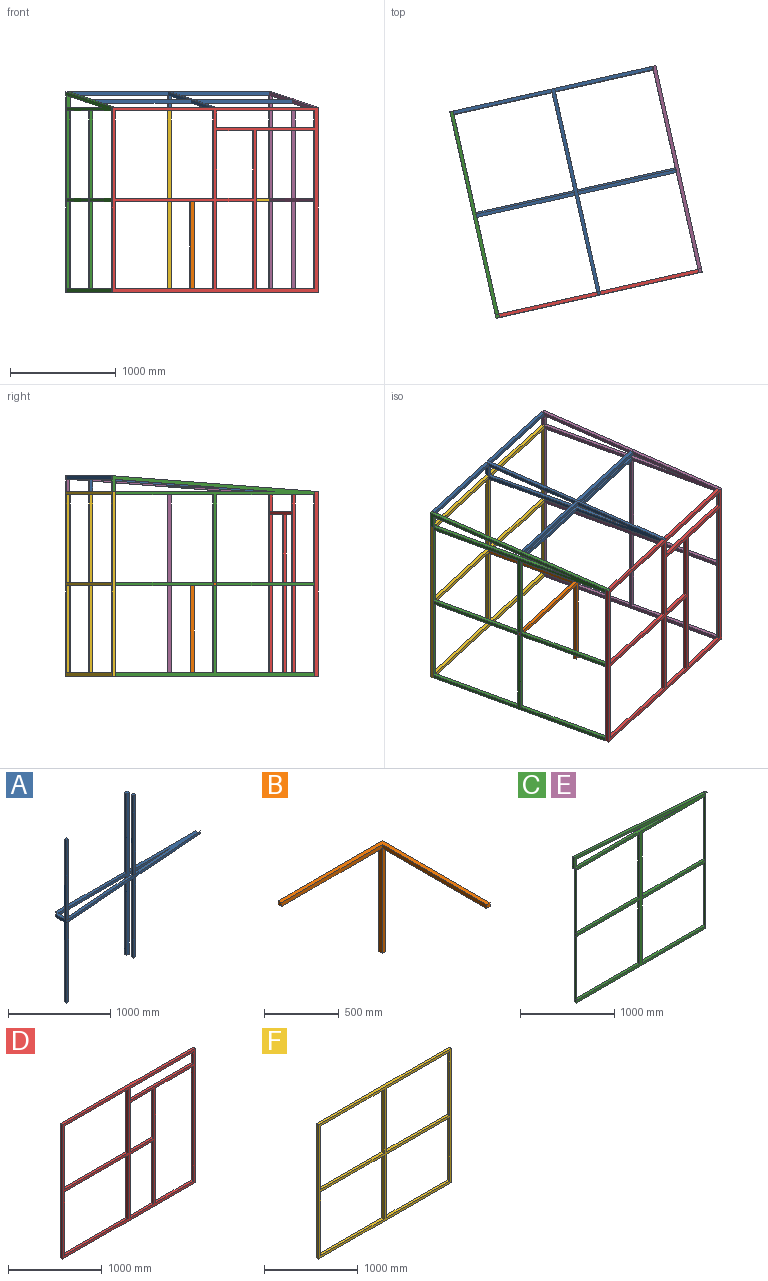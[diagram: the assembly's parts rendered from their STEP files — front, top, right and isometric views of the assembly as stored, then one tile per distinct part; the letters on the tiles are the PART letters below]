
ASSEMBLY  parts=6 mates=5
PART A: 38 faces, bbox 2000x183x1944 mm
  f0: plane 2000x183mm, normal (0,0,1), area 86723.9mm2, adj f3,f10,f11,f13,f18,f19,f20,f21
  f1: plane 984x148.51mm, normal (0,0,1), area 35116.9mm2, adj f3,f4,f5,f13,f14,f15,f16,f17
  f2: plane 2000x183mm, normal (0,0,-1), area 86723.9mm2, adj f3,f8,f10,f13,f18,f19,f20,f21
  f3: plane 1936x1537.88mm, normal (0,-1,0), area 110140.3mm2, adj f0,f1,f2,f4,f6,f7,f8,f9
  f4: plane 952x33mm, normal (-1,0,0), area 31416mm2, adj f1,f3,f12,f13
  f5: plane 33x32mm, normal (-1,0,0), area 1056mm2, adj f1,f9,f13,f14
  f6: plane 952x33mm, normal (-1,0,0), area 31416mm2, adj f3,f7,f9,f13
  f7: plane 33x32mm, normal (0,0,-1), area 1056mm2, adj f3,f6,f8,f13
  f8: plane 952x33mm, normal (1,0,0), area 31416mm2, adj f2,f3,f7,f13
  f9: plane 984x148.51mm, normal (0,0,-1), area 35116.9mm2, adj f3,f5,f6,f13,f14,f15,f16,f17
  f10: plane 33x32mm, normal (1,0,0), area 1056mm2, adj f0,f2,f13,f19
  f11: plane 952x33mm, normal (1,0,0), area 31416mm2, adj f0,f3,f12,f13
  f12: plane 33x32mm, normal (0,0,1), area 1056mm2, adj f3,f4,f11,f13
  f13: plane 1936x1936mm, normal (0,1,0), area 122880mm2, adj f0,f1,f2,f4,f5,f6,f7,f8
  f14: plane 32x32mm, normal (0,1,0), area 1024mm2, adj f1,f5,f9,f21
  f15: plane 32x2.02mm, normal (1,0,0), area 64.5mm2, adj f1,f3,f9,f16
  f16: plane 32x2.25mm, normal (0,-1,0), area 72.1mm2, adj f1,f9,f15,f17
  f17: plane 113.49x32mm, normal (1,0,0), area 3631.8mm2, adj f1,f9,f16,f18
  f18: plane 1944x1540.14mm, normal (-0.07,1,0), area 110606.7mm2, adj f0,f2,f3,f17,f26,f28,f29,f34
  f19: plane 32x32mm, normal (0,1,0), area 1024mm2, adj f0,f2,f10,f20
  f20: plane 2000x150mm, normal (0.07,-1,0), area 64179.7mm2, adj f0,f2,f19,f21
  f21: plane 1944x150mm, normal (-1,0,0), area 65984mm2, adj f0,f1,f2,f9,f14,f20,f23,f24
  f22: plane 956x32mm, normal (1,0,0), area 30592mm2, adj f2,f23,f24,f25
  f23: plane 956x32mm, normal (0,-1,0), area 30592mm2, adj f2,f21,f22,f25
  f24: plane 956x32mm, normal (0,1,0), area 30592mm2, adj f9,f21,f22,f25
  f25: plane 32x32mm, normal (0,0,-1), area 1024mm2, adj f21,f22,f23,f24
  f26: plane 956x32mm, normal (1,0,0), area 30592mm2, adj f2,f18,f27,f29
  f27: plane 956x31.91mm, normal (0.07,-1,0), area 30592mm2, adj f2,f26,f28,f29
  f28: plane 956x32mm, normal (-1,0,0), area 30592mm2, adj f2,f18,f27,f29
  f29: plane 34.39x31.91mm, normal (0,0,-1), area 1021.1mm2, adj f18,f26,f27,f28
  f30: plane 956x32mm, normal (1,0,0), area 30592mm2, adj f0,f31,f32,f33
  f31: plane 956x32mm, normal (0,-1,0), area 30592mm2, adj f0,f21,f30,f33
  f32: plane 956x32mm, normal (0,1,0), area 30592mm2, adj f1,f21,f30,f33
  f33: plane 32x32mm, normal (0,0,1), area 1024mm2, adj f21,f30,f31,f32
  f34: plane 956x32mm, normal (1,0,0), area 30592mm2, adj f0,f18,f35,f37
  f35: plane 956x31.91mm, normal (0.07,-1,0), area 30592mm2, adj f0,f34,f36,f37
  f36: plane 956x32mm, normal (-1,0,0), area 30592mm2, adj f0,f18,f35,f37
  f37: plane 34.39x31.91mm, normal (0,0,1), area 1021.1mm2, adj f18,f34,f35,f36
PART B: 12 faces, bbox 984x1017x891 mm
  f0: plane 952x32mm, normal (0,-1,0), area 30464mm2, adj f1,f2,f3,f9
  f1: plane 1017x984mm, normal (0,0,1), area 63960mm2, adj f0,f2,f6,f8,f9,f11
  f2: plane 33x32mm, normal (-1,0,0), area 1056mm2, adj f0,f1,f3,f8
  f3: plane 952x33mm, normal (0,0,-1), area 31416mm2, adj f0,f2,f4,f8
  f4: plane 859x33mm, normal (-1,0,0), area 28347mm2, adj f3,f5,f7,f8
  f5: plane 33x32mm, normal (0,0,-1), area 1056mm2, adj f4,f6,f7,f8
  f6: plane 1017x891mm, normal (1,0,0), area 60891mm2, adj f1,f5,f7,f8,f10,f11
  f7: plane 859x32mm, normal (0,-1,0), area 27488mm2, adj f4,f5,f6,f10
  f8: plane 984x891mm, normal (0,1,0), area 58976mm2, adj f1,f2,f3,f4,f5,f6
  f9: plane 984x32mm, normal (-1,0,0), area 31488mm2, adj f0,f1,f10,f11
  f10: plane 984x32mm, normal (0,0,-1), area 31488mm2, adj f6,f7,f9,f11
  f11: plane 32x32mm, normal (0,-1,0), area 1024mm2, adj f1,f6,f9,f10
PART C: 30 faces, bbox 2000x33x1900 mm
  f0: plane 33x0.87mm, normal (1,0,0), area 28.8mm2, adj f1,f27,f28,f29
  f1: plane 33x1.2mm, normal (0,0,1), area 39.7mm2, adj f0,f2,f28,f29
  f2: plane 114.64x33mm, normal (1,0,0), area 3783mm2, adj f1,f3,f28,f29
  f3: plane 1540.14x115.51mm, normal (-0.07,0,-1), area 50967.2mm2, adj f2,f27,f28,f29
  f4: plane 1936x33mm, normal (0,0,-1), area 63888mm2, adj f5,f22,f28,f29
  f5: plane 1750x33mm, normal (1,0,0), area 57750mm2, adj f4,f6,f28,f29
  f6: plane 33x32mm, normal (0,0,-1), area 1056mm2, adj f5,f7,f28,f29
  f7: plane 2000x150mm, normal (0.07,0,1), area 66185.4mm2, adj f6,f8,f28,f29
  f8: plane 150x33mm, normal (-1,0,0), area 4950mm2, adj f7,f9,f28,f29
  f9: plane 33x32mm, normal (0,0,-1), area 1056mm2, adj f8,f22,f28,f29
  f10: plane 827x33mm, normal (-1,0,0), area 27291mm2, adj f11,f23,f28,f29
  f11: plane 947.5x33mm, normal (0,0,1), area 31267.5mm2, adj f10,f12,f28,f29
  f12: plane 827x33mm, normal (1,0,0), area 27291mm2, adj f11,f23,f28,f29
  f13: plane 827x33mm, normal (1,0,0), area 27291mm2, adj f14,f24,f28,f29
  f14: plane 950.5x33mm, normal (0,0,-1), area 31366.5mm2, adj f13,f15,f28,f29
  f15: plane 827x33mm, normal (-1,0,0), area 27291mm2, adj f14,f24,f28,f29
  f16: plane 827x33mm, normal (1,0,0), area 27291mm2, adj f17,f25,f28,f29
  f17: plane 950.5x33mm, normal (0,0,-1), area 31366.5mm2, adj f16,f18,f28,f29
  f18: plane 827x33mm, normal (-1,0,0), area 27291mm2, adj f17,f25,f28,f29
  f19: plane 947.5x33mm, normal (0,0,-1), area 31267.5mm2, adj f20,f26,f28,f29
  f20: plane 827x33mm, normal (-1,0,0), area 27291mm2, adj f19,f21,f28,f29
  f21: plane 947.5x33mm, normal (0,0,1), area 31267.5mm2, adj f20,f26,f28,f29
  f22: plane 1750x33mm, normal (-1,0,0), area 57750mm2, adj f4,f9,f28,f29
  f23: plane 947.5x33mm, normal (0,0,-1), area 31267.5mm2, adj f10,f12,f28,f29
  f24: plane 950.5x33mm, normal (0,0,1), area 31366.5mm2, adj f13,f15,f28,f29
  f25: plane 950.5x33mm, normal (0,0,1), area 31366.5mm2, adj f16,f18,f28,f29
  f26: plane 827x33mm, normal (1,0,0), area 27291mm2, adj f19,f21,f28,f29
  f27: plane 1538.93x33mm, normal (0,0,1), area 50784.8mm2, adj f0,f3,f28,f29
  f28: plane 2000x1900mm, normal (0,-1,0), area 309758.5mm2, adj f0,f1,f2,f3,f4,f5,f6,f7
  f29: plane 2000x1900mm, normal (0,1,0), area 309758.5mm2, adj f0,f1,f2,f3,f4,f5,f6,f7
PART D: 30 faces, bbox 2000x32x1750 mm
  f0: plane 641x32mm, normal (1,0,0), area 20512mm2, adj f1,f27,f28,f29
  f1: plane 356x32mm, normal (0,0,-1), area 11392mm2, adj f0,f2,f28,f29
  f2: plane 641x32mm, normal (-1,0,0), area 20512mm2, adj f1,f27,f28,f29
  f3: plane 827x32mm, normal (-1,0,0), area 26464mm2, adj f4,f21,f28,f29
  f4: plane 952x32mm, normal (0,0,1), area 30464mm2, adj f3,f5,f28,f29
  f5: plane 827x32mm, normal (1,0,0), area 26464mm2, adj f4,f21,f28,f29
  f6: plane 2000x32mm, normal (0,0,1), area 64000mm2, adj f7,f22,f28,f29
  f7: plane 1750x32mm, normal (-1,0,0), area 56000mm2, adj f6,f8,f28,f29
  f8: plane 2000x32mm, normal (0,0,-1), area 64000mm2, adj f7,f22,f28,f29
  f9: plane 564x32mm, normal (0,0,1), area 18048mm2, adj f10,f23,f28,f29
  f10: plane 1500x32mm, normal (1,0,0), area 48000mm2, adj f9,f11,f28,f29
  f11: plane 564x32mm, normal (0,0,-1), area 18048mm2, adj f10,f23,f28,f29
  f12: plane 827x32mm, normal (-1,0,0), area 26464mm2, adj f13,f24,f28,f29
  f13: plane 356x32mm, normal (0,0,1), area 11392mm2, adj f12,f14,f28,f29
  f14: plane 827x32mm, normal (1,0,0), area 26464mm2, adj f13,f24,f28,f29
  f15: plane 952x32mm, normal (0,0,-1), area 30464mm2, adj f16,f25,f28,f29
  f16: plane 827x32mm, normal (-1,0,0), area 26464mm2, adj f15,f17,f28,f29
  f17: plane 952x32mm, normal (0,0,1), area 30464mm2, adj f16,f25,f28,f29
  f18: plane 154x32mm, normal (1,0,0), area 4928mm2, adj f19,f26,f28,f29
  f19: plane 952x32mm, normal (0,0,-1), area 30464mm2, adj f18,f20,f28,f29
  f20: plane 154x32mm, normal (-1,0,0), area 4928mm2, adj f19,f26,f28,f29
  f21: plane 952x32mm, normal (0,0,-1), area 30464mm2, adj f3,f5,f28,f29
  f22: plane 1750x32mm, normal (1,0,0), area 56000mm2, adj f6,f8,f28,f29
  f23: plane 1500x32mm, normal (-1,0,0), area 48000mm2, adj f9,f11,f28,f29
  f24: plane 356x32mm, normal (0,0,-1), area 11392mm2, adj f12,f14,f28,f29
  f25: plane 827x32mm, normal (1,0,0), area 26464mm2, adj f15,f17,f28,f29
  f26: plane 952x32mm, normal (0,0,1), area 30464mm2, adj f18,f20,f28,f29
  f27: plane 356x32mm, normal (0,0,1), area 11392mm2, adj f0,f2,f28,f29
  f28: plane 2000x1750mm, normal (0,-1,0), area 410176mm2, adj f0,f1,f2,f3,f4,f5,f6,f7
  f29: plane 2000x1750mm, normal (0,1,0), area 410176mm2, adj f0,f1,f2,f3,f4,f5,f6,f7
PART E: same geometry as C
PART F: 22 faces, bbox 2000x33x1750 mm
  f0: plane 827x33mm, normal (-1,0,0), area 27291mm2, adj f1,f19,f20,f21
  f1: plane 952x33mm, normal (0,0,1), area 31416mm2, adj f0,f2,f20,f21
  f2: plane 827x33mm, normal (1,0,0), area 27291mm2, adj f1,f19,f20,f21
  f3: plane 2000x33mm, normal (0,0,1), area 66000mm2, adj f4,f15,f20,f21
  f4: plane 1750x33mm, normal (-1,0,0), area 57750mm2, adj f3,f5,f20,f21
  f5: plane 2000x33mm, normal (0,0,-1), area 66000mm2, adj f4,f15,f20,f21
  f6: plane 952x33mm, normal (0,0,-1), area 31416mm2, adj f7,f16,f20,f21
  f7: plane 827x33mm, normal (-1,0,0), area 27291mm2, adj f6,f8,f20,f21
  f8: plane 952x33mm, normal (0,0,1), area 31416mm2, adj f7,f16,f20,f21
  f9: plane 952x33mm, normal (0,0,-1), area 31416mm2, adj f10,f17,f20,f21
  f10: plane 827x33mm, normal (-1,0,0), area 27291mm2, adj f9,f11,f20,f21
  f11: plane 952x33mm, normal (0,0,1), area 31416mm2, adj f10,f17,f20,f21
  f12: plane 827x33mm, normal (1,0,0), area 27291mm2, adj f13,f18,f20,f21
  f13: plane 952x33mm, normal (0,0,-1), area 31416mm2, adj f12,f14,f20,f21
  f14: plane 827x33mm, normal (-1,0,0), area 27291mm2, adj f13,f18,f20,f21
  f15: plane 1750x33mm, normal (1,0,0), area 57750mm2, adj f3,f5,f20,f21
  f16: plane 827x33mm, normal (1,0,0), area 27291mm2, adj f6,f8,f20,f21
  f17: plane 827x33mm, normal (1,0,0), area 27291mm2, adj f9,f11,f20,f21
  f18: plane 952x33mm, normal (0,0,1), area 31416mm2, adj f12,f14,f20,f21
  f19: plane 952x33mm, normal (0,0,-1), area 31416mm2, adj f0,f2,f20,f21
  f20: plane 2000x1750mm, normal (0,-1,0), area 350784mm2, adj f0,f1,f2,f3,f4,f5,f6,f7
  f21: plane 2000x1750mm, normal (0,1,0), area 350784mm2, adj f0,f1,f2,f3,f4,f5,f6,f7
PLACE A rot(axis=(-0.66,0.53,-0.53),113deg) t=(-8886.5,8172.22,1945.98)mm
PLACE B rot(axis=(0,0,-1),77.3deg) t=(-7554.47,6726.62,193.36)mm
PLACE C rot(axis=(0,0,-1),77.3deg) t=(-7986.91,4165.39,227.98)mm
PLACE D rot(axis=(0,0,1),12.7deg) t=(-7595,2269.18,227.98)mm
PLACE E rot(axis=(0,0,-1),77.3deg) t=(-6067.68,4596.28,227.98)mm
PLACE F rot(axis=(0,0,1),12.7deg) t=(-8026.33,4190.36,227.98)mm
MATE fastened C.f22 <-> F.f20  axis (-0.22,0.98,0) through (-8019.1,4158.16,227.98)mm
MATE fastened B.f2 <-> F.f20  axis (-0.22,0.98,0) through (-7027.78,4380.73,1118.98)mm
MATE fastened A.f7 <-> C.f29  axis (-0.98,-0.22,0) through (-7778.69,3237.98,1945.98)mm
MATE fastened D.f29 <-> E.f5  axis (-0.22,0.98,0) through (-5643.58,2707.31,227.98)mm
MATE fastened E.f22 <-> F.f20  axis (-0.22,0.98,0) through (-6067.68,4596.28,227.98)mm
